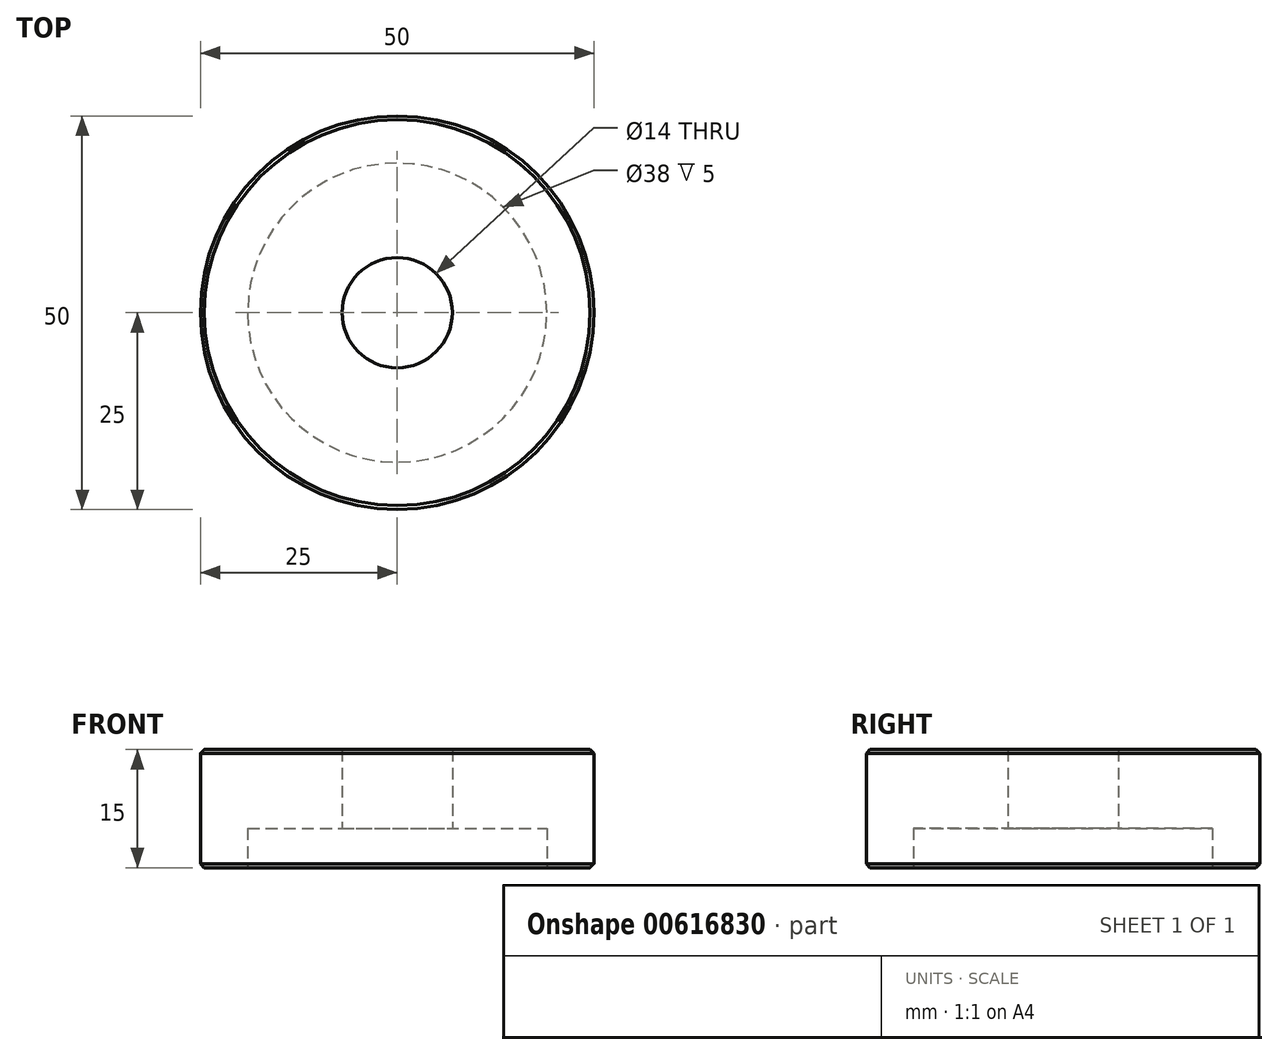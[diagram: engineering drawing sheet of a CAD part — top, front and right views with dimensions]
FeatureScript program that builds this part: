
annotation { "Feature Type Name" : "Feature", "Feature Type Description" : "" }
export const myFeature = defineFeature(function(context is Context, id is Id, definition is map)
    precondition{}
    {
        {
            var Q0;
            Q0=qCreatedBy(makeId("Front.planeOp"),FACE);
            var sketch = newSketch(context, id + "F0", { "sketchPlane" : qUnion([Q0])});
            skLineSegment(sketch, "E0", {"start": v(19, 0) * mm, "end": v(19, 5) * mm});
            skLineSegment(sketch, "E1", {"start": v(19, 5) * mm, "end": v(7, 5) * mm});
            skLineSegment(sketch, "E2", {"start": v(7, 15) * mm, "end": v(25, 15) * mm});
            skLineSegment(sketch, "E3", {"start": v(25, 15) * mm, "end": v(25, 0) * mm});
            skLineSegment(sketch, "E4", {"start": v(25, 0) * mm, "end": v(19, 0) * mm});
            skLineSegment(sketch, "E5", {"start": v(7, 15) * mm, "end": v(7, 5) * mm});
            skLineSegment(sketch, "E6", {"start": v(0, 0) * mm, "end": v(0, 37.34) * mm, "construction": true});
            skSolve(sketch);
        }
        {
            var Q0;
            Q0=makeQuery(id+"F0.imprint","IMPRINT",FACE,{"disambiguationData":[TD([[makeQuery(id+"F0.imprint","IMPRINT",EDGE,{"derivedFrom":sQuery(id+"F0.wireOp",EDGE,"E0")}),-1.0]])]});
            var Q1;
            Q1=sQuery(id+"F0.wireOp",EDGE,"E6");
            revolve(context, id + "F1", {"surfaceOperationType" : NewSurfaceOperationType.NEW, "entities" : qUnion([Q0]), "axis" : qUnion([Q1]), "revolveType" : RevolveType.FULL});
        }
        {
            var Q0;
            Q0=makeQuery(id+"F1.opRevolve","SWEPT_EDGE",EDGE,{"disambiguationData":[OSD([sQuery(id+"F0.wireOp",EDGE,"E2"),sQuery(id+"F0.wireOp",EDGE,"E3")])]});
            chamfer(context, id + "F2", {"entities" : qUnion([Q0]), "width" : 0.5 * mm, "tangentPropagation" : true});
        }
        {
            var Q0;
            Q0=makeQuery(id+"F1.opRevolve","SWEPT_EDGE",EDGE,{"disambiguationData":[OSD([sQuery(id+"F0.wireOp",EDGE,"E3"),sQuery(id+"F0.wireOp",EDGE,"E4")])]});
            chamfer(context, id + "F3", {"entities" : qUnion([Q0]), "width" : 0.5 * mm, "tangentPropagation" : true});
        }
    });
